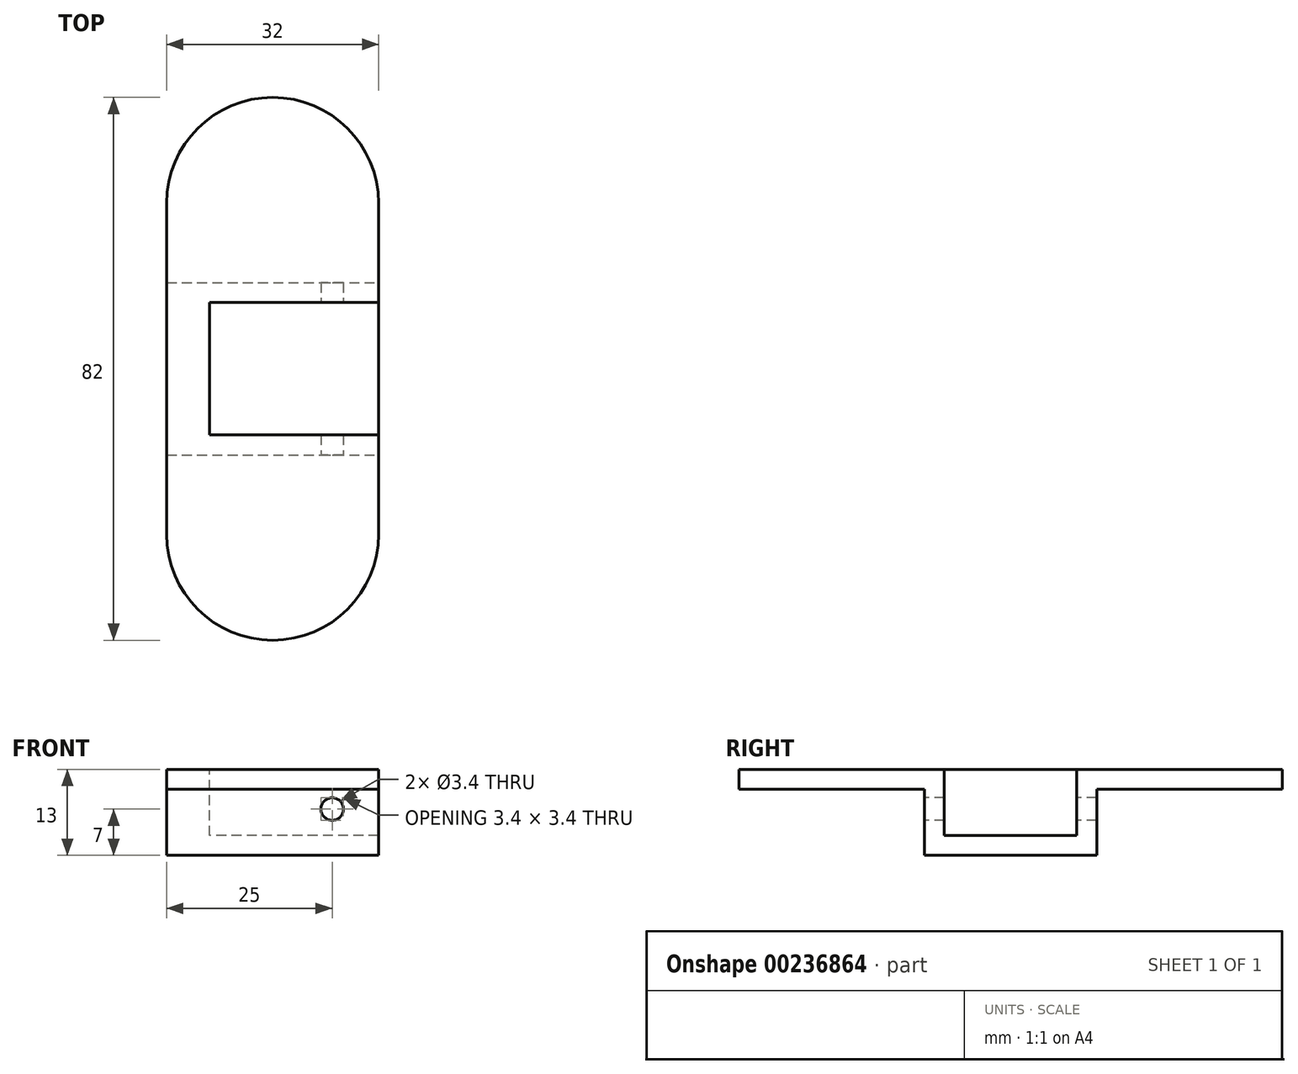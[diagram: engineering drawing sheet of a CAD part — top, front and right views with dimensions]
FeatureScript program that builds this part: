
annotation { "Feature Type Name" : "Feature", "Feature Type Description" : "" }
export const myFeature = defineFeature(function(context is Context, id is Id, definition is map)
    precondition{}
    {
        {
            var Q0;
            Q0=qCreatedBy(makeId("Top.planeOp"),FACE);
            var sketch = newSketch(context, id + "F0", { "sketchPlane" : qUnion([Q0])});
            skLineSegment(sketch, "E0", {"start": v(0, 25) * mm, "end": v(0, -25) * mm, "construction": true});
            skArc(sketch, "E1", {"start": v(16, 25) * mm, "mid": v(0, 41) * mm, "end": v(-16, 25) * mm});
            skArc(sketch, "E2", {"start": v(-16, -25) * mm, "mid": v(0, -41) * mm, "end": v(16, -25) * mm});
            skLineSegment(sketch, "E3", {"start": v(16, -25) * mm, "end": v(16, 25) * mm});
            skLineSegment(sketch, "E4", {"start": v(-16, 25) * mm, "end": v(-16, -25) * mm});
            skSolve(sketch);
        }
        {
            var Q0;
            Q0 = qSketchRegion(id + "F0", true);
            extrude(context, id + "F1", {"entities" : qUnion([Q0]), "depth" : 3 * mm});
        }
        {
            var Q0;
            Q0=makeQuery(id+"F1.opExtrude","CAP_FACE",FACE,{"disambiguationData":[OSD([sQuery(id+"F0.wireOp",EDGE,"E1"),sQuery(id+"F0.wireOp",EDGE,"E2"),sQuery(id+"F0.wireOp",EDGE,"E3"),sQuery(id+"F0.wireOp",EDGE,"E4")])],"isStart":true});
            var sketch = newSketch(context, id + "F2", { "sketchPlane" : qUnion([Q0])});
            skLineSegment(sketch, "E5.bottom", {"start": v(-16, 13) * mm, "end": v(16, 13) * mm});
            skLineSegment(sketch, "E5.top", {"start": v(-16, -13) * mm, "end": v(16, -13) * mm});
            skLineSegment(sketch, "E5.left", {"start": v(-16, 13) * mm, "end": v(-16, -13) * mm});
            skLineSegment(sketch, "E5.right", {"start": v(16, 13) * mm, "end": v(16, -13) * mm});
            skLineSegment(sketch, "E6", {"start": v(-16, 0) * mm, "end": v(16, 0) * mm, "construction": true});
            skSolve(sketch);
        }
        {
            var Q0;
            Q0 = qSketchRegion(id + "F2", true);
            extrude(context, id + "F3", {"entities" : qUnion([Q0]), "operationType" : NewBodyOperationType.ADD, "depth" : 10 * mm});
        }
        {
            var Q0;
            Q0=makeQuery(id+"F1.opExtrude","CAP_FACE",FACE,{"disambiguationData":[OSD([sQuery(id+"F0.wireOp",EDGE,"E1"),sQuery(id+"F0.wireOp",EDGE,"E2"),sQuery(id+"F0.wireOp",EDGE,"E3"),sQuery(id+"F0.wireOp",EDGE,"E4")])],"isStart":false});
            var sketch = newSketch(context, id + "F4", { "sketchPlane" : qUnion([Q0])});
            skLineSegment(sketch, "E7.bottom", {"start": v(16, 10) * mm, "end": v(-9.5, 10) * mm});
            skLineSegment(sketch, "E7.top", {"start": v(16, -10) * mm, "end": v(-9.5, -10) * mm});
            skLineSegment(sketch, "E7.left", {"start": v(16, 10) * mm, "end": v(16, -10) * mm});
            skLineSegment(sketch, "E7.right", {"start": v(-9.5, 10) * mm, "end": v(-9.5, -10) * mm});
            skLineSegment(sketch, "E8", {"start": v(0, 0) * mm, "end": v(16, 0) * mm, "construction": true});
            skSolve(sketch);
        }
        {
            var Q0;
            Q0 = qSketchRegion(id + "F4", true);
            extrude(context, id + "F5", {"entities" : qUnion([Q0]), "operationType" : NewBodyOperationType.REMOVE, "oppositeDirection" : true, "depth" : 10 * mm});
        }
        {
            var Q0;
            Q0=makeQuery(id+"F3.opExtrude","SWEPT_FACE",FACE,{"disambiguationData":[OSD([sQuery(id+"F2.wireOp",EDGE,"E5.bottom")])]});
            var sketch = newSketch(context, id + "F6", { "sketchPlane" : qUnion([Q0])});
            skCircle(sketch, "E9", {"center": v(9, -3) * mm, "radius": 1.7 * mm});
            skSolve(sketch);
        }
        {
            var Q0;
            Q0 = qSketchRegion(id + "F6", true);
            extrude(context, id + "F7", {"entities" : qUnion([Q0]), "operationType" : NewBodyOperationType.REMOVE, "oppositeDirection" : true, "depth" : 101.6 * mm});
        }
    });
